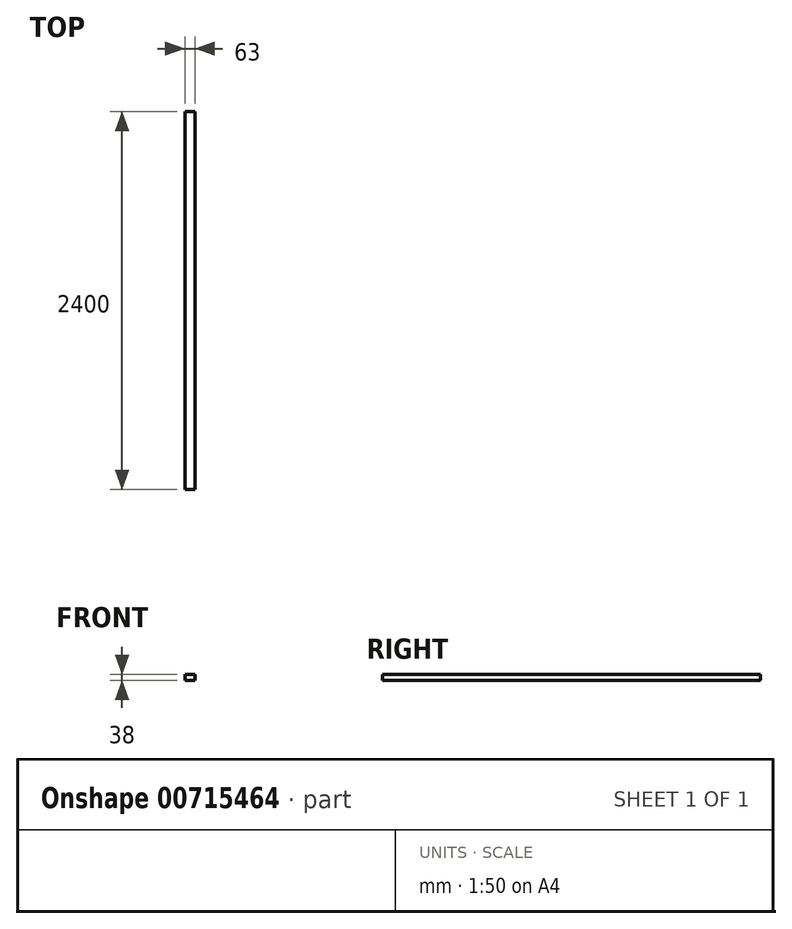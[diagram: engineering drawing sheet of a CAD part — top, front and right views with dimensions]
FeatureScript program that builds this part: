
annotation { "Feature Type Name" : "Feature", "Feature Type Description" : "" }
export const myFeature = defineFeature(function(context is Context, id is Id, definition is map)
    precondition{}
    {
        {
            var Q0;
            Q0=qCreatedBy(makeId("Front.planeOp"),FACE);
            var sketch = newSketch(context, id + "F0", { "sketchPlane" : qUnion([Q0])});
            skLineSegment(sketch, "E0.bottom", {"start": v(31.5, 19) * mm, "end": v(-31.5, 19) * mm});
            skLineSegment(sketch, "E0.top", {"start": v(31.5, -19) * mm, "end": v(-31.5, -19) * mm});
            skLineSegment(sketch, "E0.left", {"start": v(31.5, 19) * mm, "end": v(31.5, -19) * mm});
            skLineSegment(sketch, "E0.right", {"start": v(-31.5, 19) * mm, "end": v(-31.5, -19) * mm});
            skPoint(sketch, "E0.middle", {"position": v(0, 0) * mm});
            skSolve(sketch);
        }
        {
            var Q0;
            Q0 = qSketchRegion(id + "F0", true);
            extrude(context, id + "F1", {"entities" : qUnion([Q0]), "depth" : 2400 * mm, "offsetDistance" : 25 * mm});
        }
    });
